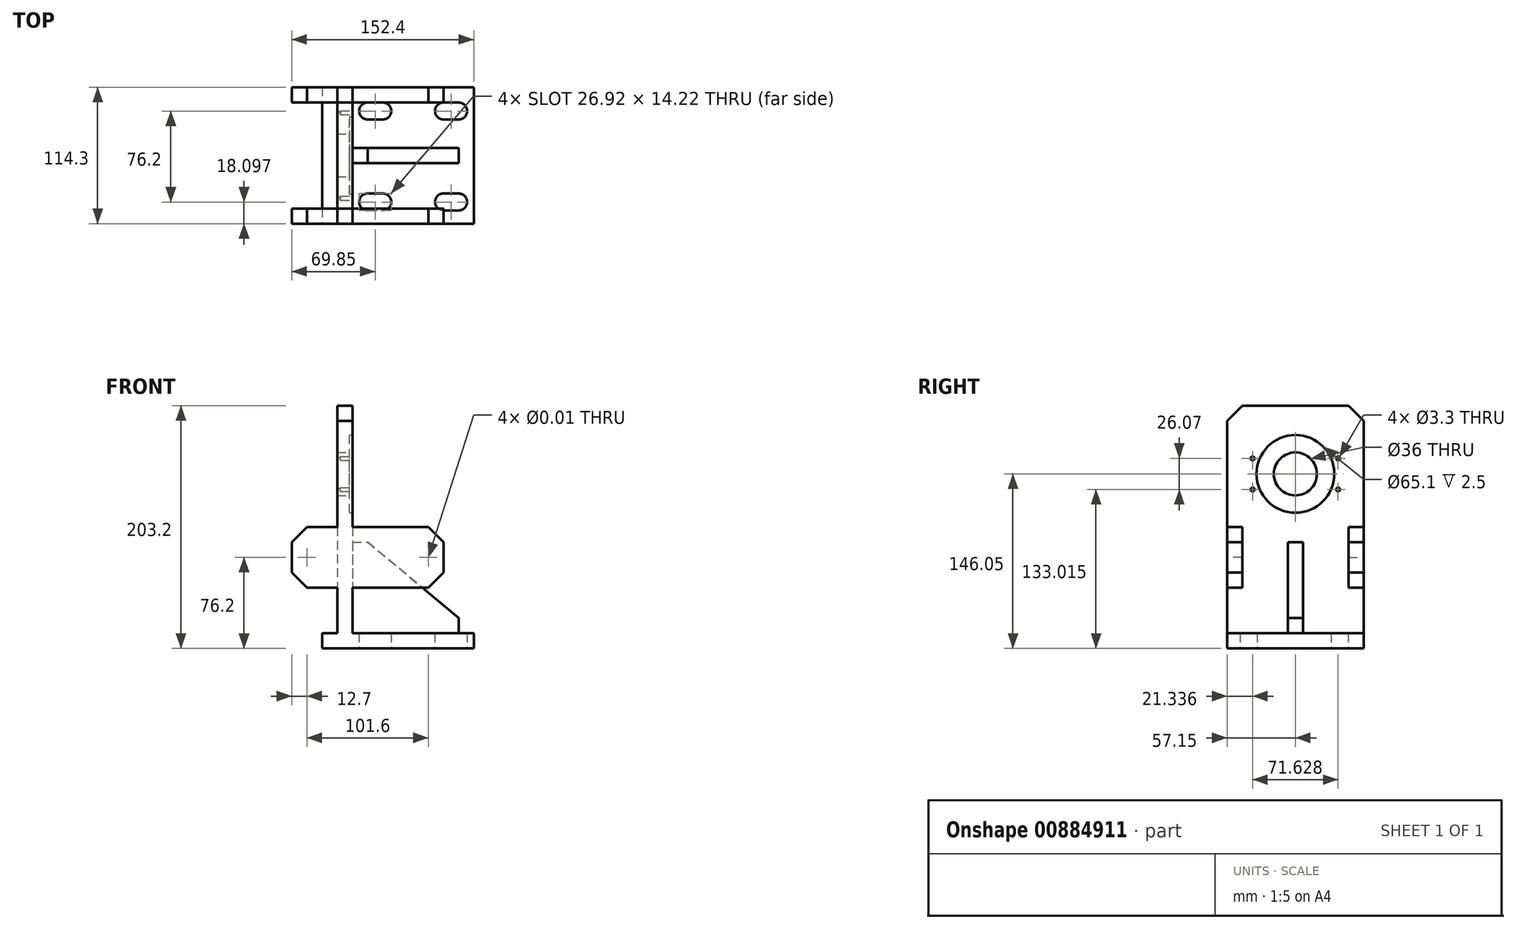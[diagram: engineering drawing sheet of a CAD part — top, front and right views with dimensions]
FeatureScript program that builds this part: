
annotation { "Feature Type Name" : "Feature", "Feature Type Description" : "" }
export const myFeature = defineFeature(function(context is Context, id is Id, definition is map)
    precondition{}
    {
        {
            var Q0;
            Q0=qCreatedBy(makeId("Top.planeOp"),FACE);
            var sketch = newSketch(context, id + "F0", { "sketchPlane" : qUnion([Q0])});
            skLineSegment(sketch, "E0.bottom", {"start": v(-63.5, 57.15) * mm, "end": v(63.5, 57.15) * mm});
            skLineSegment(sketch, "E0.top", {"start": v(-63.5, -57.15) * mm, "end": v(63.5, -57.15) * mm});
            skLineSegment(sketch, "E0.left", {"start": v(-63.5, 57.15) * mm, "end": v(-63.5, -57.15) * mm});
            skLineSegment(sketch, "E0.right", {"start": v(63.5, 57.15) * mm, "end": v(63.5, -57.15) * mm});
            skPoint(sketch, "E0.middle", {"position": v(0, 0) * mm});
            skLineSegment(sketch, "E1.0", {"start": v(44.45, 57.15) * mm, "end": v(44.45, -57.15) * mm, "construction": true});
            skLineSegment(sketch, "E2", {"start": v(38.1, 37.15) * mm, "end": v(50.8, 37.15) * mm, "construction": true});
            skArc(sketch, "E3.0.startCap", {"start": v(38.1, 30.04) * mm, "mid": v(30.99, 37.15) * mm, "end": v(38.1, 44.26) * mm});
            skArc(sketch, "E3.0.endCap", {"start": v(50.8, 44.26) * mm, "mid": v(57.91, 37.15) * mm, "end": v(50.8, 30.04) * mm});
            skLineSegment(sketch, "E3.0.left", {"start": v(38.1, 44.26) * mm, "end": v(50.8, 44.26) * mm});
            skLineSegment(sketch, "E3.0.right", {"start": v(38.1, 30.04) * mm, "end": v(50.8, 30.04) * mm});
            skLineSegment(sketch, "E4.0.1.0", {"start": v(38.1, -31.94) * mm, "end": v(50.8, -31.94) * mm});
            skArc(sketch, "E4.0.1.1", {"start": v(38.1, -46.16) * mm, "mid": v(30.99, -39.05) * mm, "end": v(38.1, -31.94) * mm});
            skArc(sketch, "E4.0.1.2", {"start": v(50.8, -31.94) * mm, "mid": v(57.91, -39.05) * mm, "end": v(50.8, -46.16) * mm});
            skLineSegment(sketch, "E4.0.1.3", {"start": v(38.1, -46.16) * mm, "end": v(50.8, -46.16) * mm});
            skLineSegment(sketch, "E4.0.1.4", {"start": v(38.1, -39.05) * mm, "end": v(50.8, -39.05) * mm, "construction": true});
            skLineSegment(sketch, "E4.1.0.0", {"start": v(-25.4, 44.26) * mm, "end": v(-12.7, 44.26) * mm});
            skArc(sketch, "E4.1.0.1", {"start": v(-25.4, 30.04) * mm, "mid": v(-32.51, 37.15) * mm, "end": v(-25.4, 44.26) * mm});
            skArc(sketch, "E4.1.0.2", {"start": v(-12.7, 44.26) * mm, "mid": v(-5.59, 37.15) * mm, "end": v(-12.7, 30.04) * mm});
            skLineSegment(sketch, "E4.1.0.3", {"start": v(-25.4, 30.04) * mm, "end": v(-12.7, 30.04) * mm});
            skLineSegment(sketch, "E4.1.0.4", {"start": v(-25.4, 37.15) * mm, "end": v(-12.7, 37.15) * mm, "construction": true});
            skLineSegment(sketch, "E4.1.1.0", {"start": v(-25.4, -31.94) * mm, "end": v(-12.7, -31.94) * mm});
            skArc(sketch, "E4.1.1.1", {"start": v(-25.4, -46.16) * mm, "mid": v(-32.51, -39.05) * mm, "end": v(-25.4, -31.94) * mm});
            skArc(sketch, "E4.1.1.2", {"start": v(-12.7, -31.94) * mm, "mid": v(-5.59, -39.05) * mm, "end": v(-12.7, -46.16) * mm});
            skLineSegment(sketch, "E4.1.1.3", {"start": v(-25.4, -46.16) * mm, "end": v(-12.7, -46.16) * mm});
            skLineSegment(sketch, "E4.1.1.4", {"start": v(-25.4, -39.05) * mm, "end": v(-12.7, -39.05) * mm, "construction": true});
            skLineSegment(sketch, "E4.direction1", {"start": v(38.1, 30.04) * mm, "end": v(-25.4, 30.04) * mm, "construction": true});
            skLineSegment(sketch, "E4.direction2", {"start": v(38.1, 30.04) * mm, "end": v(38.1, -46.16) * mm, "construction": true});
            skSolve(sketch);
        }
        {
            var Q0;
            Q0 = qSketchRegion(id + "F0", true);
            extrude(context, id + "F1", {"entities" : qUnion([Q0]), "depth" : 12.7 * mm, "offsetDistance" : 25.4 * mm});
        }
        {
            var Q0;
            Q0=makeQuery(id+"F1.opExtrude","CAP_FACE",FACE,{"disambiguationData":[OSD([sQuery(id+"F0.wireOp",EDGE,"E0.bottom"),sQuery(id+"F0.wireOp",EDGE,"E0.top"),sQuery(id+"F0.wireOp",EDGE,"E0.left"),sQuery(id+"F0.wireOp",EDGE,"E0.right"),sQuery(id+"F0.wireOp",EDGE,"E3.0.startCap"),sQuery(id+"F0.wireOp",EDGE,"E3.0.endCap"),sQuery(id+"F0.wireOp",EDGE,"E3.0.left"),sQuery(id+"F0.wireOp",EDGE,"E3.0.right"),sQuery(id+"F0.wireOp",EDGE,"E4.0.1.0"),sQuery(id+"F0.wireOp",EDGE,"E4.0.1.1"),sQuery(id+"F0.wireOp",EDGE,"E4.0.1.2"),sQuery(id+"F0.wireOp",EDGE,"E4.0.1.3"),sQuery(id+"F0.wireOp",EDGE,"E4.1.0.0"),sQuery(id+"F0.wireOp",EDGE,"E4.1.0.1"),sQuery(id+"F0.wireOp",EDGE,"E4.1.0.2"),sQuery(id+"F0.wireOp",EDGE,"E4.1.0.3"),sQuery(id+"F0.wireOp",EDGE,"E4.1.1.0"),sQuery(id+"F0.wireOp",EDGE,"E4.1.1.1"),sQuery(id+"F0.wireOp",EDGE,"E4.1.1.2"),sQuery(id+"F0.wireOp",EDGE,"E4.1.1.3")])],"isStart":false});
            var sketch = newSketch(context, id + "F2", { "sketchPlane" : qUnion([Q0])});
            skLineSegment(sketch, "E5.bottom", {"start": v(-50.8, 57.15) * mm, "end": v(-38.1, 57.15) * mm});
            skLineSegment(sketch, "E5.top", {"start": v(-50.8, -57.15) * mm, "end": v(-38.1, -57.15) * mm});
            skLineSegment(sketch, "E5.left", {"start": v(-50.8, 57.15) * mm, "end": v(-50.8, -57.15) * mm});
            skLineSegment(sketch, "E5.right", {"start": v(-38.1, 57.15) * mm, "end": v(-38.1, -57.15) * mm});
            skSolve(sketch);
        }
        {
            var Q0;
            Q0 = qSketchRegion(id + "F2", true);
            extrude(context, id + "F3", {"entities" : qUnion([Q0]), "operationType" : NewBodyOperationType.ADD, "depth" : 190.5 * mm, "offsetDistance" : 25.4 * mm});
        }
        {
            var Q0;
            Q0=makeQuery(id+"F3.opExtrude","CAP_EDGE",EDGE,{"disambiguationData":[OSD([sQuery(id+"F2.wireOp",EDGE,"E5.bottom")])],"isStart":false});
            var Q1;
            Q1=makeQuery(id+"F3.opExtrude","CAP_EDGE",EDGE,{"disambiguationData":[OSD([sQuery(id+"F2.wireOp",EDGE,"E5.top")])],"isStart":false});
            chamfer(context, id + "F4", {"entities" : qUnion([Q0, Q1]), "width" : 12.7 * mm, "tangentPropagation" : true});
        }
        {
            var Q0;
            Q0=makeQuery(id+"F3.opExtrude","SWEPT_FACE",FACE,{"disambiguationData":[OSD([sQuery(id+"F2.wireOp",EDGE,"E5.right")])]});
            var sketch = newSketch(context, id + "F5", { "sketchPlane" : qUnion([Q0])});
            skLineSegment(sketch, "E6", {"start": v(0, 12.7) * mm, "end": v(0, 146.05) * mm, "construction": true});
            skPoint(sketch, "E7", {"position": v(0, 146.05) * mm});
            skSolve(sketch);
        }
        {
            var Q0;
            Q0=sQuery(id+"F5.wireOp",VERTEX,"E7");
            var Q1;
            Q1=makeQuery(id+"F1.opExtrude","SWEPT_BODY",BODY,{"disambiguationData":[OSD([sQuery(id+"F0.wireOp",EDGE,"E0.bottom"),sQuery(id+"F0.wireOp",EDGE,"E0.top"),sQuery(id+"F0.wireOp",EDGE,"E0.left"),sQuery(id+"F0.wireOp",EDGE,"E0.right"),sQuery(id+"F0.wireOp",EDGE,"E3.0.startCap"),sQuery(id+"F0.wireOp",EDGE,"E3.0.endCap"),sQuery(id+"F0.wireOp",EDGE,"E3.0.left"),sQuery(id+"F0.wireOp",EDGE,"E3.0.right"),sQuery(id+"F0.wireOp",EDGE,"E4.0.1.0"),sQuery(id+"F0.wireOp",EDGE,"E4.0.1.1"),sQuery(id+"F0.wireOp",EDGE,"E4.0.1.2"),sQuery(id+"F0.wireOp",EDGE,"E4.0.1.3"),sQuery(id+"F0.wireOp",EDGE,"E4.1.0.0"),sQuery(id+"F0.wireOp",EDGE,"E4.1.0.1"),sQuery(id+"F0.wireOp",EDGE,"E4.1.0.2"),sQuery(id+"F0.wireOp",EDGE,"E4.1.0.3"),sQuery(id+"F0.wireOp",EDGE,"E4.1.1.0"),sQuery(id+"F0.wireOp",EDGE,"E4.1.1.1"),sQuery(id+"F0.wireOp",EDGE,"E4.1.1.2"),sQuery(id+"F0.wireOp",EDGE,"E4.1.1.3")])]});
            hole(context, id + "F6", {"style" : HoleStyle.C_BORE, "endStyle" : HoleEndStyle.THROUGH, "holeDiameter" : 36 * mm, "cBoreDiameter" : 65.1 * mm, "cBoreDepth" : 2.5 * mm, "majorDiameter" : 6.35 * mm, "isTappedThrough" : true, "tappedDepth" : 38.1 * mm, "tapClearance" : 3, "startFromSketch" : true, "locations" : qUnion([Q0]), "scope" : qUnion([Q1])});
        }
        {
            var Q0;
            Q0=makeQuery(id+"F3.opExtrude","SWEPT_FACE",FACE,{"disambiguationData":[OSD([sQuery(id+"F2.wireOp",EDGE,"E5.right")])]});
            var sketch = newSketch(context, id + "F7", { "sketchPlane" : qUnion([Q0])});
            skCircle(sketch, "E8.0", {"center": v(0, 146.05) * mm, "radius": 32.55 * mm, "construction": true});
            skLineSegment(sketch, "E9", {"start": v(0, 146.05) * mm, "end": v(-107.1, 146.05) * mm, "construction": true});
            skLineSegment(sketch, "E10", {"start": v(0, 146.05) * mm, "end": v(-106.15, 107.41) * mm, "construction": true});
            skLineSegment(sketch, "E11", {"start": v(0, 146.05) * mm, "end": v(0, -42.62) * mm, "construction": true});
            skLineSegment(sketch, "E12.0", {"start": v(-35.81, 146.05) * mm, "end": v(-35.81, -42.62) * mm, "construction": true});
            skPoint(sketch, "E13", {"position": v(-35.81, 133.01) * mm});
            skPoint(sketch, "E14.MirrorP", {"position": v(-35.81, 159.09) * mm});
            skPoint(sketch, "E15.MirrorP", {"position": v(35.81, 159.09) * mm});
            skPoint(sketch, "E16.MirrorP", {"position": v(35.81, 133.01) * mm});
            skSolve(sketch);
        }
        {
            var Q0;
            Q0=sQuery(id+"F7.wireOp",VERTEX,"E14.MirrorP");
            var Q1;
            Q1=sQuery(id+"F7.wireOp",VERTEX,"E13");
            var Q2;
            Q2=sQuery(id+"F7.wireOp",VERTEX,"E16.MirrorP");
            var Q3;
            Q3=sQuery(id+"F7.wireOp",VERTEX,"E15.MirrorP");
            var Q4;
            Q4=makeQuery(id+"F1.opExtrude","SWEPT_BODY",BODY,{"disambiguationData":[OSD([sQuery(id+"F0.wireOp",EDGE,"E0.bottom"),sQuery(id+"F0.wireOp",EDGE,"E0.top"),sQuery(id+"F0.wireOp",EDGE,"E0.left"),sQuery(id+"F0.wireOp",EDGE,"E0.right"),sQuery(id+"F0.wireOp",EDGE,"E3.0.startCap"),sQuery(id+"F0.wireOp",EDGE,"E3.0.endCap"),sQuery(id+"F0.wireOp",EDGE,"E3.0.left"),sQuery(id+"F0.wireOp",EDGE,"E3.0.right"),sQuery(id+"F0.wireOp",EDGE,"E4.0.1.0"),sQuery(id+"F0.wireOp",EDGE,"E4.0.1.1"),sQuery(id+"F0.wireOp",EDGE,"E4.0.1.2"),sQuery(id+"F0.wireOp",EDGE,"E4.0.1.3"),sQuery(id+"F0.wireOp",EDGE,"E4.1.0.0"),sQuery(id+"F0.wireOp",EDGE,"E4.1.0.1"),sQuery(id+"F0.wireOp",EDGE,"E4.1.0.2"),sQuery(id+"F0.wireOp",EDGE,"E4.1.0.3"),sQuery(id+"F0.wireOp",EDGE,"E4.1.1.0"),sQuery(id+"F0.wireOp",EDGE,"E4.1.1.1"),sQuery(id+"F0.wireOp",EDGE,"E4.1.1.2"),sQuery(id+"F0.wireOp",EDGE,"E4.1.1.3")])]});
            hole(context, id + "F8", {"style" : HoleStyle.SIMPLE, "endStyle" : HoleEndStyle.BLIND, "standardTappedOrClearance" : lookupTablePath({ "standard" : "ISO", "engagement" : "75%", "pitch" : "0.7 mm", "size" : "M4", "type" : "Tapped" }), "standardBlindInLast" : lookupTablePath({ "standard" : "ISO", "engagement" : "75%", "pitch" : "0.7 mm", "size" : "M4", "type" : "Tapped" }), "holeDiameter" : 3.3 * mm, "majorDiameter" : 4 * mm, "showTappedDepth" : true, "holeDepth" : 10 * mm, "isTappedThrough" : true, "tappedDepth" : 7.9 * mm, "tapClearance" : 3, "startFromSketch" : true, "locations" : qUnion([Q0, Q1, Q2, Q3]), "scope" : qUnion([Q4])});
        }
        {
            var Q0;
            Q0=makeQuery(id+"F3.boolean.opBoolean","MERGE",FACE,{"derivedFrom":[makeQuery(id+"F1.opExtrude","SWEPT_FACE",FACE,{"disambiguationData":[OSD([sQuery(id+"F0.wireOp",EDGE,"E0.top")])]}),makeQuery(id+"F3.opExtrude","SWEPT_FACE",FACE,{"disambiguationData":[OSD([sQuery(id+"F2.wireOp",EDGE,"E5.top")])]})]});
            var sketch = newSketch(context, id + "F9", { "sketchPlane" : qUnion([Q0])});
            skLineSegment(sketch, "E17.0", {"start": v(-38.1, 190.5) * mm, "end": v(-38.1, 12.7) * mm, "construction": true});
            skLineSegment(sketch, "E18.0", {"start": v(-50.8, 190.5) * mm, "end": v(-50.8, 12.7) * mm, "construction": true});
            skLineSegment(sketch, "E19.0", {"start": v(-63.5, 50.8) * mm, "end": v(63.5, 50.8) * mm, "construction": true});
            skLineSegment(sketch, "E20.bottom", {"start": v(-50.8, 50.8) * mm, "end": v(-88.9, 50.8) * mm});
            skLineSegment(sketch, "E20.top", {"start": v(-50.8, 101.6) * mm, "end": v(-88.9, 101.6) * mm});
            skLineSegment(sketch, "E20.left", {"start": v(-50.8, 50.8) * mm, "end": v(-50.8, 101.6) * mm});
            skLineSegment(sketch, "E20.right", {"start": v(-88.9, 50.8) * mm, "end": v(-88.9, 101.6) * mm});
            skLineSegment(sketch, "E21.bottom", {"start": v(-38.1, 50.8) * mm, "end": v(38.1, 50.8) * mm});
            skLineSegment(sketch, "E21.top", {"start": v(-38.1, 101.6) * mm, "end": v(38.1, 101.6) * mm});
            skLineSegment(sketch, "E21.left", {"start": v(-38.1, 50.8) * mm, "end": v(-38.1, 101.6) * mm});
            skLineSegment(sketch, "E21.right", {"start": v(38.1, 50.8) * mm, "end": v(38.1, 101.6) * mm});
            skSolve(sketch);
        }
        {
            var Q0;
            Q0 = qSketchRegion(id + "F9", true);
            extrude(context, id + "F10", {"entities" : qUnion([Q0]), "oppositeDirection" : true, "depth" : 12.7 * mm, "offsetDistance" : 25.4 * mm});
        }
        {
            var Q0;
            Q0=makeQuery(id+"F10.opExtrude","SWEPT_EDGE",EDGE,{"disambiguationData":[OSD([sQuery(id+"F9.wireOp",EDGE,"E20.top"),sQuery(id+"F9.wireOp",EDGE,"E20.right")])]});
            var Q1;
            Q1=makeQuery(id+"F10.opExtrude","SWEPT_EDGE",EDGE,{"disambiguationData":[OSD([sQuery(id+"F9.wireOp",EDGE,"E20.bottom"),sQuery(id+"F9.wireOp",EDGE,"E20.right")])]});
            var Q2;
            Q2=makeQuery(id+"F10.opExtrude","SWEPT_EDGE",EDGE,{"disambiguationData":[OSD([sQuery(id+"F9.wireOp",EDGE,"E21.top"),sQuery(id+"F9.wireOp",EDGE,"E21.right")])]});
            var Q3;
            Q3=makeQuery(id+"F10.opExtrude","SWEPT_EDGE",EDGE,{"disambiguationData":[OSD([sQuery(id+"F9.wireOp",EDGE,"E21.bottom"),sQuery(id+"F9.wireOp",EDGE,"E21.right")])]});
            chamfer(context, id + "F11", {"entities" : qUnion([Q0, Q1, Q2, Q3]), "width" : 12.7 * mm, "tangentPropagation" : true});
        }
        {
            var Q0;
            Q0=makeQuery(id+"F10.opExtrude","CAP_FACE",FACE,{"disambiguationData":[OSD([sQuery(id+"F9.wireOp",EDGE,"E20.bottom"),sQuery(id+"F9.wireOp",EDGE,"E20.top"),sQuery(id+"F9.wireOp",EDGE,"E20.left"),sQuery(id+"F9.wireOp",EDGE,"E20.right")])],"isStart":true});
            var sketch = newSketch(context, id + "F12", { "sketchPlane" : qUnion([Q0])});
            skLineSegment(sketch, "E22", {"start": v(-76.2, 101.6) * mm, "end": v(-76.2, 50.8) * mm, "construction": true});
            skLineSegment(sketch, "E23.0", {"start": v(-38.1, 101.6) * mm, "end": v(25.4, 101.6) * mm, "construction": true});
            skLineSegment(sketch, "E24.0", {"start": v(-38.1, 50.8) * mm, "end": v(25.4, 50.8) * mm, "construction": true});
            skLineSegment(sketch, "E25", {"start": v(25.4, 101.6) * mm, "end": v(25.4, 50.8) * mm, "construction": true});
            skPoint(sketch, "E26", {"position": v(-76.2, 76.2) * mm});
            skPoint(sketch, "E27", {"position": v(25.4, 76.2) * mm});
            skSolve(sketch);
        }
        {
            var Q0;
            Q0=sQuery(id+"F12.wireOp",VERTEX,"E26");
            var Q1;
            Q1=sQuery(id+"F12.wireOp",VERTEX,"E27");
            var Q2;
            Q2=makeQuery(id+"F10.opExtrude","SWEPT_BODY",BODY,{"disambiguationData":[OSD([sQuery(id+"F9.wireOp",EDGE,"E20.bottom"),sQuery(id+"F9.wireOp",EDGE,"E20.top"),sQuery(id+"F9.wireOp",EDGE,"E20.left"),sQuery(id+"F9.wireOp",EDGE,"E20.right")])]});
            var Q3;
            Q3=makeQuery(id+"F10.opExtrude","SWEPT_BODY",BODY,{"disambiguationData":[OSD([sQuery(id+"F9.wireOp",EDGE,"E21.bottom"),sQuery(id+"F9.wireOp",EDGE,"E21.top"),sQuery(id+"F9.wireOp",EDGE,"E21.left"),sQuery(id+"F9.wireOp",EDGE,"E21.right")])]});
            hole(context, id + "F13", {"style" : HoleStyle.SIMPLE, "endStyle" : HoleEndStyle.THROUGH, "standardTappedOrClearance" : lookupTablePath({ "standard" : "ANSI", "size" : "5/16 (0.31)", "type" : "Drilled" }), "standardBlindInLast" : lookupTablePath({ "standard" : "ANSI", "size" : "5/16", "type" : "Drilled" }), "holeDiameter" : 5 / 406.4 * mm, "majorDiameter" : 6.35 * mm, "isTappedThrough" : true, "tappedDepth" : 7.9 * mm, "tapClearance" : 3, "startFromSketch" : true, "locations" : qUnion([Q0, Q1]), "scope" : qUnion([Q2, Q3])});
        }
        {
            var Q0;
            Q0=makeQuery(id+"F10.opExtrude","SWEPT_BODY",BODY,{"disambiguationData":[OSD([sQuery(id+"F9.wireOp",EDGE,"E21.bottom"),sQuery(id+"F9.wireOp",EDGE,"E21.top"),sQuery(id+"F9.wireOp",EDGE,"E21.left"),sQuery(id+"F9.wireOp",EDGE,"E21.right")])]});
            var Q1;
            Q1=makeQuery(id+"F10.opExtrude","SWEPT_BODY",BODY,{"disambiguationData":[OSD([sQuery(id+"F9.wireOp",EDGE,"E20.bottom"),sQuery(id+"F9.wireOp",EDGE,"E20.top"),sQuery(id+"F9.wireOp",EDGE,"E20.left"),sQuery(id+"F9.wireOp",EDGE,"E20.right")])]});
            var Q2;
            Q2=qCreatedBy(makeId("Front.planeOp"),FACE);
            mirror(context, id + "F14", {"operationType" : NewBodyOperationType.ADD, "entities" : qUnion([Q0, Q1]), "mirrorPlane" : qUnion([Q2])});
        }
        {
            var Q0;
            {var subQ0=sQuery(id+"F0.wireOp",EDGE,"E4.0.1.2");var subQ1=sQuery(id+"F0.wireOp",EDGE,"E4.0.1.0");var subQ2=sQuery(id+"F0.wireOp",EDGE,"E3.0.right");var subQ3=sQuery(id+"F0.wireOp",EDGE,"E3.0.left");var subQ4=sQuery(id+"F0.wireOp",EDGE,"E3.0.endCap");var subQ5=sQuery(id+"F0.wireOp",EDGE,"E4.0.1.1");var subQ6=sQuery(id+"F0.wireOp",EDGE,"E0.bottom");var subQ7=sQuery(id+"F0.wireOp",EDGE,"E0.right");var subQ8=sQuery(id+"F0.wireOp",EDGE,"E0.top");var subQ9=sQuery(id+"F0.wireOp",EDGE,"E3.0.startCap");var subQ10=sQuery(id+"F0.wireOp",EDGE,"E4.0.1.3");var subQ11=sQuery(id+"F0.wireOp",EDGE,"E4.1.0.0");var subQ12=sQuery(id+"F0.wireOp",EDGE,"E4.1.0.1");var subQ13=sQuery(id+"F0.wireOp",EDGE,"E4.1.0.2");var subQ14=sQuery(id+"F0.wireOp",EDGE,"E4.1.0.3");var subQ15=sQuery(id+"F0.wireOp",EDGE,"E4.1.1.0");var subQ16=sQuery(id+"F0.wireOp",EDGE,"E4.1.1.1");var subQ17=sQuery(id+"F0.wireOp",EDGE,"E4.1.1.2");var subQ18=sQuery(id+"F0.wireOp",EDGE,"E4.1.1.3");Q0=makeQuery(id+"F3.boolean.opBoolean","SPLIT",FACE,{"disambiguationData":[TD([makeQuery(id+"F1.opExtrude","SWEPT_FACE",FACE,{"disambiguationData":[OSD([subQ7])]})])],"derivedFrom":makeQuery(id+"F1.opExtrude","CAP_FACE",FACE,{"disambiguationData":[OSD([subQ6,subQ8,sQuery(id+"F0.wireOp",EDGE,"E0.left"),subQ7,subQ9,subQ4,subQ3,subQ2,subQ1,subQ5,subQ0,subQ10,subQ11,subQ12,subQ13,subQ14,subQ15,subQ16,subQ17,subQ18])],"isStart":false})});}
            var sketch = newSketch(context, id + "F15", { "sketchPlane" : qUnion([Q0])});
            skLineSegment(sketch, "E28.0", {"start": v(-38.1, 44.45) * mm, "end": v(-38.1, -44.45) * mm, "construction": true});
            skLineSegment(sketch, "E29", {"start": v(-38.1, 0) * mm, "end": v(6.35, 0) * mm, "construction": true});
            skLineSegment(sketch, "E30.bottom", {"start": v(-38.1, 6.35) * mm, "end": v(50.8, 6.35) * mm});
            skLineSegment(sketch, "E30.top", {"start": v(-38.1, -6.35) * mm, "end": v(50.8, -6.35) * mm});
            skLineSegment(sketch, "E30.left", {"start": v(-38.1, 6.35) * mm, "end": v(-38.1, -6.35) * mm});
            skLineSegment(sketch, "E30.right", {"start": v(50.8, 6.35) * mm, "end": v(50.8, -6.35) * mm});
            skPoint(sketch, "E30.middle", {"position": v(6.35, 0) * mm});
            skSolve(sketch);
        }
        {
            var Q0;
            Q0 = qSketchRegion(id + "F15", true);
            extrude(context, id + "F16", {"entities" : qUnion([Q0]), "operationType" : NewBodyOperationType.ADD, "depth" : 76.2 * mm, "offsetDistance" : 25.4 * mm});
        }
        {
            var Q0;
            Q0=makeQuery(id+"F16.opExtrude","CAP_EDGE",EDGE,{"disambiguationData":[OSD([sQuery(id+"F15.wireOp",EDGE,"E30.right")])],"isStart":false});
            chamfer(context, id + "F17", {"entities" : qUnion([Q0]), "chamferType" : ChamferType.TWO_OFFSETS, "width1" : 63.5 * mm, "oppositeDirection" : false, "width2" : 76.2 * mm, "tangentPropagation" : true});
        }
    });
